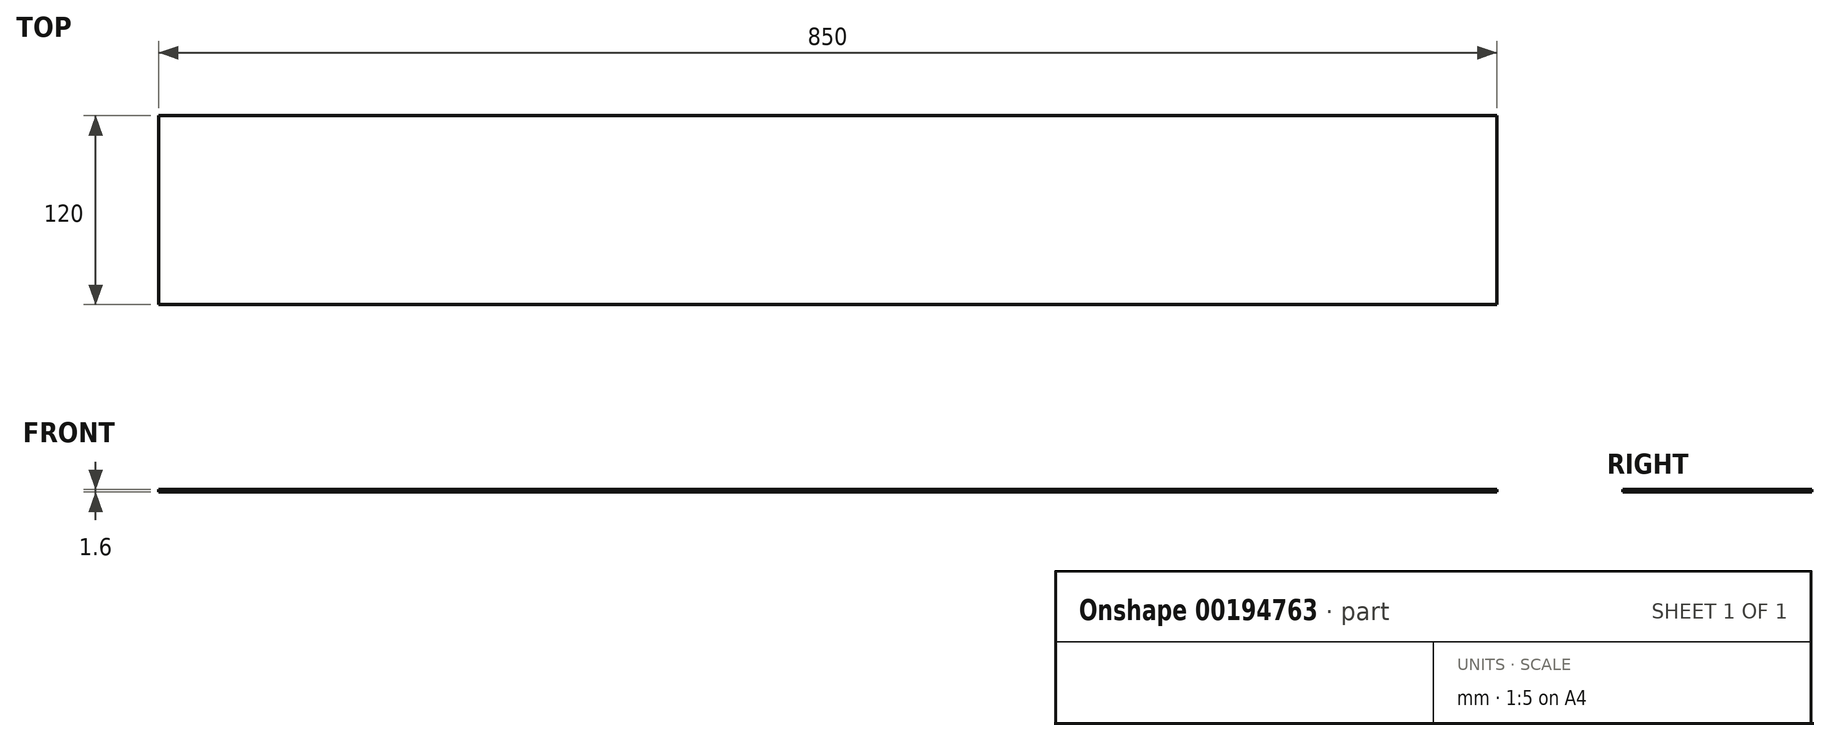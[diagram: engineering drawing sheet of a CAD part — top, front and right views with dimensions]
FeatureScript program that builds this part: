
annotation { "Feature Type Name" : "Feature", "Feature Type Description" : "" }
export const myFeature = defineFeature(function(context is Context, id is Id, definition is map)
    precondition{}
    {
        {
            var Q0;
            Q0=qCreatedBy(makeId("Top.planeOp"),FACE);
            var sketch = newSketch(context, id + "F0", { "sketchPlane" : qUnion([Q0])});
            skLineSegment(sketch, "E0.bottom", {"start": v(425, 60) * mm, "end": v(-425, 60) * mm});
            skLineSegment(sketch, "E0.top", {"start": v(425, -60) * mm, "end": v(-425, -60) * mm});
            skLineSegment(sketch, "E0.left", {"start": v(425, 60) * mm, "end": v(425, -60) * mm});
            skLineSegment(sketch, "E0.right", {"start": v(-425, 60) * mm, "end": v(-425, -60) * mm});
            skPoint(sketch, "E0.middle", {"position": v(0, 0) * mm});
            skSolve(sketch);
        }
        {
            var Q0;
            Q0 = qSketchRegion(id + "F0", true);
            extrude(context, id + "F1", {"entities" : qUnion([Q0]), "depth" : 1.6 * mm});
        }
    });
